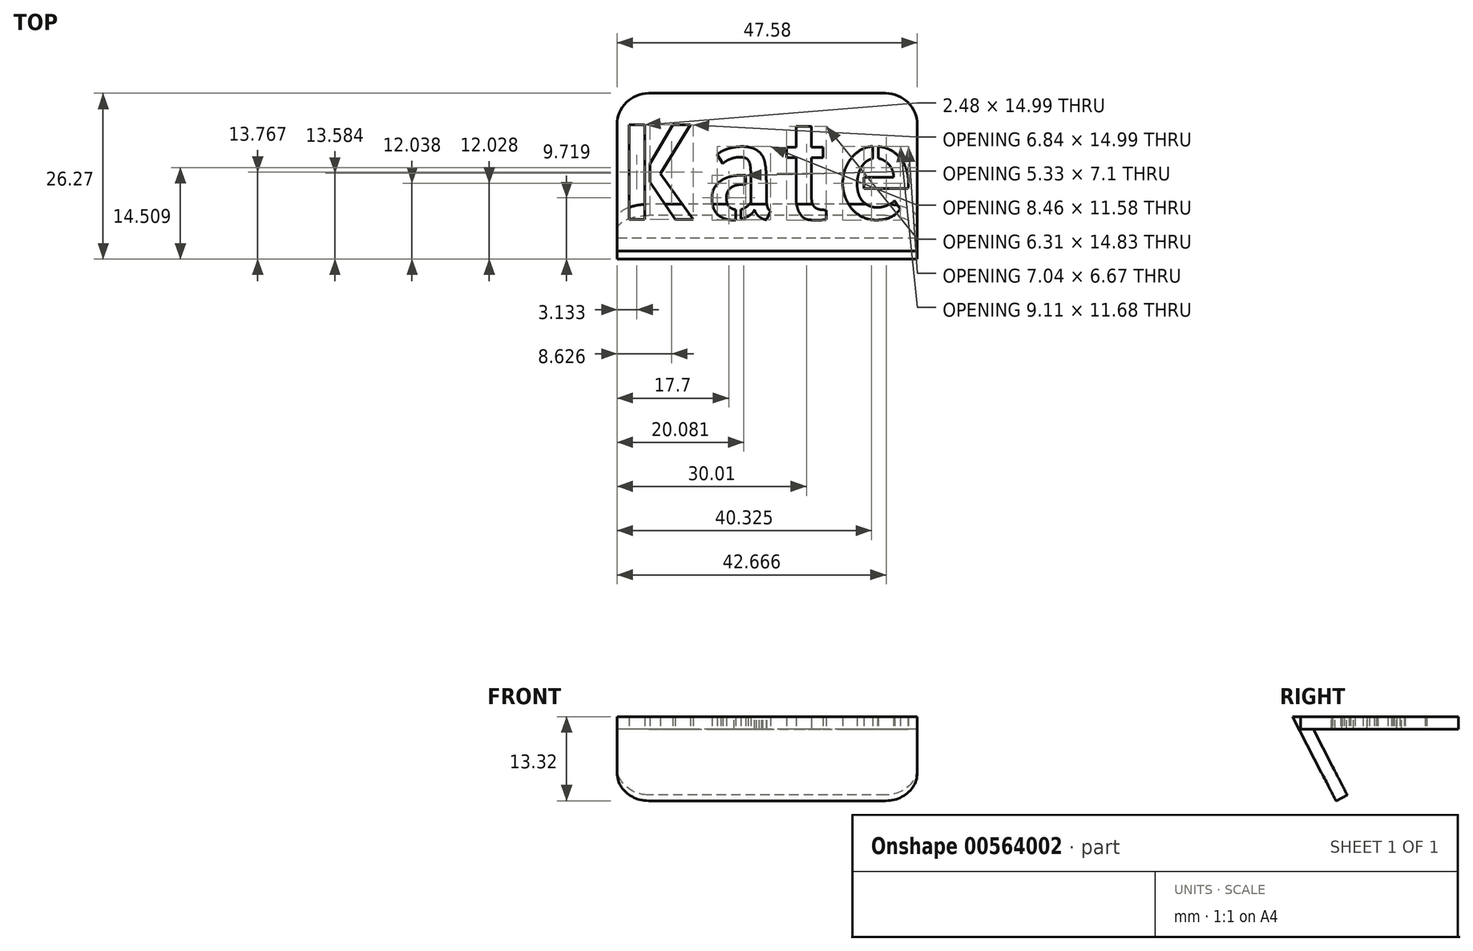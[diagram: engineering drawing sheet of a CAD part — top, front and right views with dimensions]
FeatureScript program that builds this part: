
annotation { "Feature Type Name" : "Feature", "Feature Type Description" : "" }
export const myFeature = defineFeature(function(context is Context, id is Id, definition is map)
    precondition{}
    {
        {
            var Q0;
            Q0=qCreatedBy(makeId("Top.planeOp"),FACE);
            var sketch = newSketch(context, id + "F0", { "sketchPlane" : qUnion([Q0])});
            skLineSegment(sketch, "E0.bottom", {"start": v(-23.58, 12.5) * mm, "end": v(24, 12.5) * mm});
            skLineSegment(sketch, "E0.top", {"start": v(-23.58, -12.5) * mm, "end": v(24, -12.5) * mm});
            skLineSegment(sketch, "E0.left", {"start": v(-23.58, 12.5) * mm, "end": v(-23.58, -12.5) * mm});
            skLineSegment(sketch, "E0.right", {"start": v(24, 12.5) * mm, "end": v(24, -12.5) * mm});
            skText(sketch, "E1", { "text": "Kate", "fontName": "AllertaStencil-Regular.ttf"});
            const initialGuessF0  = {"E1": [-0.02358, -0.0075, 1, 0, 0.015]};
            skSetInitialGuess(sketch, initialGuessF0);
            skSolve(sketch);
        }
        {
            var Q0;
            Q0=makeQuery(id+"F0.imprint","IMPRINT",FACE,{"disambiguationData":[TD([[makeQuery(id+"F0.imprint","IMPRINT",EDGE,{"derivedFrom":sQuery(id+"F0.wireOp",EDGE,"E0.bottom")}),-1.0]])]});
            extrude(context, id + "F1", {"entities" : qUnion([Q0]), "depth" : 2 * mm, "offsetDistance" : 25 * mm});
        }
        {
            var Q0;
            {var subQ0=sQuery(id+"F0.wireOp",EDGE,"E0.left");Q0=makeQuery(id+"FYEOEdhl7jzHk82_2.opBoolean","MERGE",FACE,{"derivedFrom":[makeQuery(id+"F1.opExtrude","SWEPT_FACE",FACE,{"disambiguationData":[OSD([subQ0])]}),makeQuery(id+"FOv1BJgTRWeWuMw_1.opExtrude","CAP_FACE",FACE,{"disambiguationData":[OSD([sQuery(id+"F0.wireOp",EDGE,"E0.bottom"),subQ0,sQuery(id+"Fjco5yBOxZZxTCI_1.wireOp",EDGE,"TpTMtmOo-qoIM-rLEy-p7IH-mKgsBanMGF23"),sQuery(id+"Fjco5yBOxZZxTCI_1.wireOp",EDGE,"Ja6BvVoQ-cpFi-Lcom-cL8s-5xC4kZiynyNl"),sQuery(id+"Fjco5yBOxZZxTCI_1.wireOp",EDGE,"utNyaJ8P-FD6r-AD7x-tpFW-fHytfVhziHLl"),sQuery(id+"Fjco5yBOxZZxTCI_1.wireOp",EDGE,"xGzW29bi-H5H8-ObLh-gdKj-mSPkAtMAUUzO")])],"isStart":true})]});}
            var sketch = newSketch(context, id + "F2", { "sketchPlane" : qUnion([Q0])});
            skLineSegment(sketch, "E2", {"start": v(11.52, 2) * mm, "end": v(5.09, -10.4) * mm});
            skLineSegment(sketch, "E3", {"start": v(5.09, -10.4) * mm, "end": v(6.87, -11.32) * mm});
            skLineSegment(sketch, "E4", {"start": v(6.87, -11.32) * mm, "end": v(13.77, 2) * mm});
            skLineSegment(sketch, "E5", {"start": v(13.77, 2) * mm, "end": v(11.52, 2) * mm});
            skSolve(sketch);
        }
        {
            var Q0;
            {var subQ4=sQuery(id+"F2.wireOp",EDGE,"E3");Q0=makeQuery(id+"F2.imprint","IMPRINT",FACE,{"disambiguationData":[TD([[makeQuery(id+"F2.imprint","IMPRINT",EDGE,{"derivedFrom":subQ4}),1.0]])]});}
            var Q1;
            Q1=makeQuery(id+"F1.opExtrude","SWEPT_FACE",FACE,{"disambiguationData":[OSD([sQuery(id+"F0.wireOp",EDGE,"E0.right")])]});
            extrude(context, id + "F3", {"entities" : qUnion([Q0]), "endBound" : BoundingType.UP_TO_SURFACE, "oppositeDirection" : true, "depth" : 75 * mm, "endBoundEntityFace" : qUnion([Q1]), "offsetDistance" : 25 * mm});
        }
        {
            var Q0;
            Q0=makeQuery(id+"F1.opExtrude","SWEPT_EDGE",EDGE,{"disambiguationData":[OSD([sQuery(id+"F0.wireOp",EDGE,"E0.bottom"),sQuery(id+"F0.wireOp",EDGE,"E0.left")])]});
            var Q1;
            Q1=makeQuery(id+"F1.opExtrude","SWEPT_EDGE",EDGE,{"disambiguationData":[OSD([sQuery(id+"F0.wireOp",EDGE,"E0.bottom"),sQuery(id+"F0.wireOp",EDGE,"E0.right")])]});
            var Q2;
            Q2=makeQuery(id+"F3.opExtrude","CAP_EDGE",EDGE,{"disambiguationData":[OSD([sQuery(id+"F2.wireOp",EDGE,"E3")])],"isStart":false});
            var Q3;
            Q3=makeQuery(id+"F3.opExtrude","CAP_EDGE",EDGE,{"disambiguationData":[OSD([sQuery(id+"F2.wireOp",EDGE,"E3")])],"isStart":true});
            var Q4;
            Q4=makeQuery(id+"F3.opExtrude","TWEAK_EDGE",EDGE,{"derivedFrom":[makeQuery(id+"F1.opExtrude","SWEPT_FACE",FACE,{"disambiguationData":[OSD([sQuery(id+"F0.wireOp",EDGE,"E0.right")])]}),makeQuery(id+"F2.imprint","IMPRINT",EDGE,{"derivedFrom":sQuery(id+"F2.wireOp",EDGE,"E3")})]});
            fillet(context, id + "F4", {"entities" : qUnion([Q0, Q1, Q2, Q3, Q4]), "radius" : 5 * mm, "tangentPropagation" : true, "allowEdgeOverflow" : false});
        }
    });
